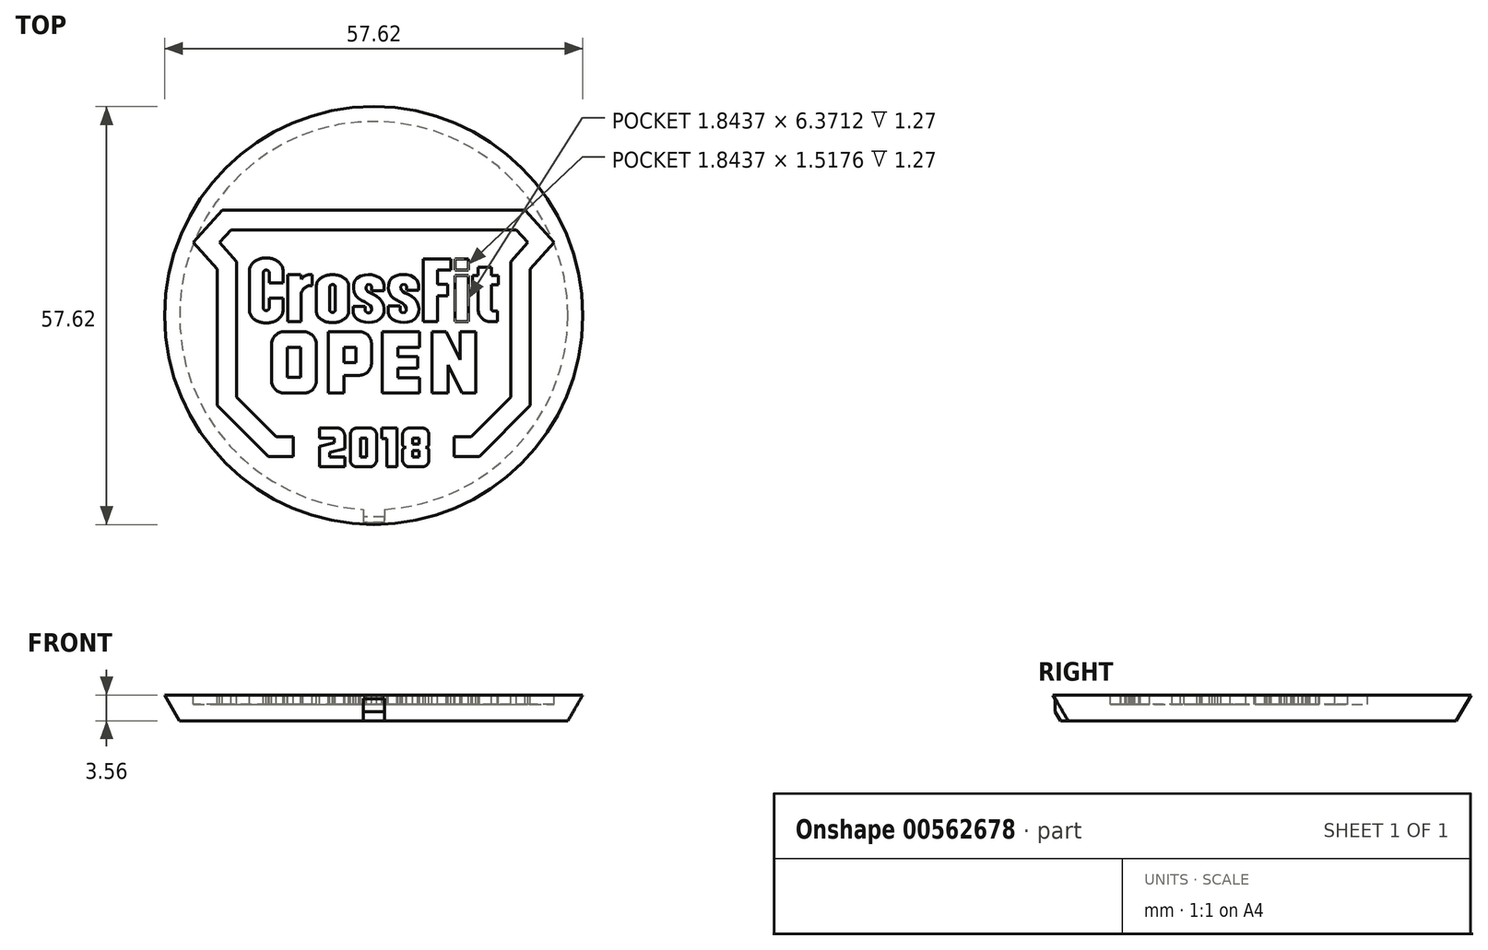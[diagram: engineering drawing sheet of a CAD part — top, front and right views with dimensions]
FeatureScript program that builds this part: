
annotation { "Feature Type Name" : "Feature", "Feature Type Description" : "" }
export const myFeature = defineFeature(function(context is Context, id is Id, definition is map)
    precondition{}
    {
        {
            var Q0;
            Q0=qCreatedBy(makeId("Top.planeOp"),FACE);
            var sketch = newSketch(context, id + "F0", { "sketchPlane" : qUnion([Q0])});
            skCircle(sketch, "E0", {"center": v(0, 0) * mm, "radius": 28.96 * mm});
            skSolve(sketch);
        }
        {
            var Q0;
            Q0=makeQuery(id+"F0.imprint","IMPRINT",FACE,{"disambiguationData":[TD([[makeQuery(id+"F0.imprint","IMPRINT",EDGE,{"derivedFrom":sQuery(id+"F0.wireOp",EDGE,"E0")}),1.0]])]});
            extrude(context, id + "F1", {"entities" : qUnion([Q0]), "depth" : 3.56 * mm, "offsetDistance" : 25.4 * mm});
        }
        {
            var Q0;
            Q0=makeQuery(id+"F1.opExtrude","CAP_FACE",FACE,{"disambiguationData":[OSD([sQuery(id+"F0.wireOp",EDGE,"E0")])],"isStart":false});
            var sketch = newSketch(context, id + "F2", { "sketchPlane" : qUnion([Q0])});
            skPoint(sketch, "E1", {"position": v(0.13, -0.67) * mm});
            skLineSegment(sketch, "E2", {"start": v(-15.2, 14.53) * mm, "end": v(-15.2, 11.82) * mm});
            skLineSegment(sketch, "E3", {"start": v(-15.2, 11.82) * mm, "end": v(-19.67, 11.82) * mm});
            skLineSegment(sketch, "E4", {"start": v(-19.67, 11.82) * mm, "end": v(-21.25, 10.06) * mm});
            skLineSegment(sketch, "E5", {"start": v(-21.25, 10.06) * mm, "end": v(-18.9, 7.43) * mm});
            skLineSegment(sketch, "E6", {"start": v(-18.9, 7.43) * mm, "end": v(-18.9, -11.25) * mm});
            skLineSegment(sketch, "E7", {"start": v(-18.9, -11.25) * mm, "end": v(-13.44, -16.74) * mm});
            skLineSegment(sketch, "E8", {"start": v(-13.44, -16.74) * mm, "end": v(-11.07, -16.74) * mm});
            skLineSegment(sketch, "E9", {"start": v(-11.07, -16.74) * mm, "end": v(-11.07, -19.45) * mm});
            skLineSegment(sketch, "E10", {"start": v(-11.07, -19.45) * mm, "end": v(-14.54, -19.45) * mm});
            skLineSegment(sketch, "E11", {"start": v(-14.54, -19.45) * mm, "end": v(-21.55, -12.4) * mm});
            skLineSegment(sketch, "E12", {"start": v(-21.55, -12.4) * mm, "end": v(-21.55, 6.37) * mm});
            skLineSegment(sketch, "E13", {"start": v(-21.55, 6.37) * mm, "end": v(-24.85, 10.06) * mm});
            skLineSegment(sketch, "E14", {"start": v(-24.85, 10.06) * mm, "end": v(-20.84, 14.53) * mm});
            skLineSegment(sketch, "E15", {"start": v(-20.84, 14.53) * mm, "end": v(-15.2, 14.53) * mm});
            skLineSegment(sketch, "E16", {"start": v(-14.42, 6) * mm, "end": v(-14.42, 4.47) * mm});
            skLineSegment(sketch, "E17", {"start": v(-14.42, 4.47) * mm, "end": v(-12.48, 4.47) * mm});
            skLineSegment(sketch, "E18", {"start": v(-12.48, 4.47) * mm, "end": v(-12.48, 6.3) * mm});
            skLineSegment(sketch, "E19", {"start": v(-17.15, 6.3) * mm, "end": v(-17.15, 0.62) * mm});
            skLineSegment(sketch, "E20", {"start": v(-14.42, 1) * mm, "end": v(-14.42, 2.43) * mm});
            skLineSegment(sketch, "E21", {"start": v(-14.42, 2.43) * mm, "end": v(-12.48, 2.43) * mm});
            skLineSegment(sketch, "E22", {"start": v(-12.48, 2.43) * mm, "end": v(-12.48, 0.62) * mm});
            skLineSegment(sketch, "E23", {"start": v(-15.2, 6) * mm, "end": v(-15.2, 1) * mm});
            skArc(sketch, "E24", {"start": v(-14.42, 6) * mm, "mid": v(-14.81, 6.27) * mm, "end": v(-15.2, 6) * mm});
            skArc(sketch, "E25", {"start": v(-15.2, 1) * mm, "mid": v(-14.81, 0.68) * mm, "end": v(-14.42, 1) * mm});
            skLineSegment(sketch, "E26", {"start": v(-9.97, 5) * mm, "end": v(-10.1, 5.63) * mm});
            skLineSegment(sketch, "E27", {"start": v(-10.1, 5.63) * mm, "end": v(-11.83, 5.63) * mm});
            skLineSegment(sketch, "E28", {"start": v(-11.83, 5.63) * mm, "end": v(-11.83, -0.85) * mm});
            skLineSegment(sketch, "E29", {"start": v(-11.83, -0.85) * mm, "end": v(-9.98, -0.85) * mm});
            skLineSegment(sketch, "E30", {"start": v(-9.98, -0.85) * mm, "end": v(-9.98, 3.1) * mm});
            skLineSegment(sketch, "E31", {"start": v(-8.5, 5.65) * mm, "end": v(-8.5, 4.11) * mm});
            skArc(sketch, "E32", {"start": v(-8.5, 5.65) * mm, "mid": v(-9.32, 5.53) * mm, "end": v(-9.97, 5) * mm});
            skArc(sketch, "E33", {"start": v(-8.5, 4.11) * mm, "mid": v(-9.44, 3.9) * mm, "end": v(-9.98, 3.1) * mm});
            skLineSegment(sketch, "E34", {"start": v(-7.89, 4.2) * mm, "end": v(-7.89, 0.46) * mm});
            skLineSegment(sketch, "E35", {"start": v(-3.47, 4.2) * mm, "end": v(-3.47, 0.46) * mm});
            skLineSegment(sketch, "E36", {"start": v(-6.05, 4.04) * mm, "end": v(-6.05, 0.68) * mm});
            skLineSegment(sketch, "E37", {"start": v(-5.3, 0.68) * mm, "end": v(-5.3, 4.04) * mm});
            skArc(sketch, "E38", {"start": v(-5.3, 4.04) * mm, "mid": v(-5.68, 4.28) * mm, "end": v(-6.05, 4.04) * mm});
            skArc(sketch, "E39", {"start": v(-6.05, 0.68) * mm, "mid": v(-5.68, 0.43) * mm, "end": v(-5.3, 0.68) * mm});
            skLineSegment(sketch, "E40", {"start": v(-5.68, 3.86) * mm, "end": v(-5.68, 0.84) * mm, "construction": true});
            skLineSegment(sketch, "E41", {"start": v(-7.89, 2.33) * mm, "end": v(-3.47, 2.33) * mm, "construction": true});
            skFitSpline(sketch, "E42.MirrorCS", {"points": [v(-3.47, 4.2) * mm, v(-3.93, 5.06) * mm, v(-4.62, 5.46) * mm, v(-5.68, 5.64) * mm], "startDerivative": vector(-0.46, 3.85) * mm, "endDerivative": vector(-4.22, 0.16) * mm});
            skFitSpline(sketch, "E43.MirrorCS", {"points": [v(-7.89, 0.46) * mm, v(-7.42, -0.4) * mm, v(-6.74, -0.8) * mm, v(-5.68, -0.98) * mm], "startDerivative": vector(0.46, -3.85) * mm, "endDerivative": vector(4.22, -0.16) * mm});
            skFitSpline(sketch, "E44.MirrorCS", {"points": [v(-3.47, 0.46) * mm, v(-3.93, -0.4) * mm, v(-4.62, -0.8) * mm, v(-5.68, -0.98) * mm], "startDerivative": vector(-0.46, -3.85) * mm, "endDerivative": vector(-4.22, -0.16) * mm});
            skFitSpline(sketch, "E45", {"points": [v(-17.15, 6.3) * mm, v(-16.64, 7.26) * mm, v(-16, 7.69) * mm, v(-14.81, 7.96) * mm], "startDerivative": vector(0.97, 4.15) * mm, "endDerivative": vector(4.22, 0.16) * mm});
            skLineSegment(sketch, "E46", {"start": v(-14.81, 5.84) * mm, "end": v(-14.81, 1.08) * mm, "construction": true});
            skFitSpline(sketch, "E47.MirrorCS", {"points": [v(-12.48, 6.3) * mm, v(-12.99, 7.26) * mm, v(-13.62, 7.69) * mm, v(-14.81, 7.96) * mm], "startDerivative": vector(-0.97, 4.15) * mm, "endDerivative": vector(-4.22, 0.16) * mm});
            skLineSegment(sketch, "E48", {"start": v(-17.15, 3.46) * mm, "end": v(-14.81, 3.46) * mm, "construction": true});
            skFitSpline(sketch, "E49.MirrorCS", {"points": [v(-17.15, 0.62) * mm, v(-16.64, -0.34) * mm, v(-16, -0.77) * mm, v(-14.81, -1.04) * mm], "startDerivative": vector(0.97, -4.15) * mm, "endDerivative": vector(4.22, -0.16) * mm});
            skFitSpline(sketch, "E50.MirrorCS", {"points": [v(-12.48, 0.62) * mm, v(-12.99, -0.34) * mm, v(-13.62, -0.77) * mm, v(-14.81, -1.04) * mm], "startDerivative": vector(-0.97, -4.15) * mm, "endDerivative": vector(-4.22, -0.16) * mm});
            skFitSpline(sketch, "E51.MirrorCS", {"points": [v(-7.89, 4.2) * mm, v(-7.42, 5.06) * mm, v(-6.74, 5.46) * mm, v(-5.68, 5.64) * mm], "startDerivative": vector(0.46, 3.85) * mm, "endDerivative": vector(4.22, 0.16) * mm});
            skLineSegment(sketch, "E52", {"start": v(-0.27, 4.07) * mm, "end": v(-0.27, 3.44) * mm});
            skLineSegment(sketch, "E53", {"start": v(-0.27, 3.44) * mm, "end": v(1.39, 3.44) * mm});
            skLineSegment(sketch, "E54", {"start": v(1.39, 3.44) * mm, "end": v(1.39, 4.25) * mm});
            skFitSpline(sketch, "E55", {"points": [v(1.39, 4.25) * mm, v(1.25, 4.73) * mm, v(0.96, 5.08) * mm, v(0.56, 5.36) * mm, v(0, 5.56) * mm, v(-0.4, 5.63) * mm, v(-0.7, 5.64) * mm, v(-1.07, 5.62) * mm, v(-1.62, 5.53) * mm, v(-2.03, 5.35) * mm, v(-2.4, 5.07) * mm, v(-2.62, 4.73) * mm, v(-2.76, 4.31) * mm, v(-2.8, 3.96) * mm, v(-2.78, 3.56) * mm, v(-2.7, 3.15) * mm, v(-2.47, 2.72) * mm, v(-2.25, 2.47) * mm, v(-1.97, 2.27) * mm, v(-1.61, 2.07) * mm, v(-1.3, 1.9) * mm, v(-1.02, 1.76) * mm, v(-0.75, 1.6) * mm, v(-0.5, 1.4) * mm, v(-0.41, 1.28) * mm, v(-0.32, 1.08) * mm, v(-0.3, 0.79) * mm, v(-0.34, 0.57) * mm, v(-0.46, 0.43) * mm, v(-0.64, 0.38) * mm, v(-0.84, 0.39) * mm, v(-1.03, 0.44) * mm, v(-1.16, 0.63) * mm], "startDerivative": vector(-2.14, 14.98) * mm, "endDerivative": vector(-3.94, 13.1) * mm});
            skLineSegment(sketch, "E56", {"start": v(-2.83, 0.39) * mm, "end": v(-2.83, 1.28) * mm});
            skLineSegment(sketch, "E57", {"start": v(-2.83, 1.28) * mm, "end": v(-1.16, 1.28) * mm});
            skLineSegment(sketch, "E58", {"start": v(-1.16, 1.28) * mm, "end": v(-1.16, 0.63) * mm});
            skFitSpline(sketch, "E59", {"points": [v(-2.83, 0.39) * mm, v(-2.67, -0.07) * mm, v(-2.35, -0.45) * mm, v(-1.98, -0.69) * mm, v(-1.5, -0.86) * mm, v(-1.03, -0.94) * mm, v(-0.7, -0.95) * mm, v(-0.34, -0.94) * mm, v(0.21, -0.84) * mm, v(0.6, -0.67) * mm, v(0.97, -0.39) * mm, v(1.22, -0.06) * mm, v(1.37, 0.3) * mm, v(1.42, 0.75) * mm, v(1.4, 1.11) * mm, v(1.3, 1.54) * mm, v(1.1, 1.95) * mm, v(0.87, 2.26) * mm, v(0.6, 2.5) * mm, v(0.3, 2.7) * mm, v(0, 2.88) * mm, v(-0.33, 3.05) * mm, v(-0.58, 3.18) * mm, v(-0.81, 3.31) * mm, v(-0.96, 3.44) * mm, v(-1.07, 3.64) * mm, v(-1.08, 3.86) * mm, v(-1.06, 4.07) * mm, v(-0.94, 4.24) * mm, v(-0.75, 4.3) * mm, v(-0.56, 4.29) * mm, v(-0.4, 4.23) * mm, v(-0.27, 4.07) * mm], "startDerivative": vector(2.14, -14.98) * mm, "endDerivative": vector(3.94, -13.1) * mm});
            skLineSegment(sketch, "E60", {"start": v(4.54, 4.08) * mm, "end": v(4.54, 3.45) * mm});
            skLineSegment(sketch, "E61", {"start": v(4.54, 3.45) * mm, "end": v(6.2, 3.45) * mm});
            skLineSegment(sketch, "E62", {"start": v(6.2, 3.45) * mm, "end": v(6.2, 4.26) * mm});
            skFitSpline(sketch, "E63", {"points": [v(6.2, 4.26) * mm, v(6.06, 4.74) * mm, v(5.77, 5.1) * mm, v(5.37, 5.37) * mm, v(4.81, 5.57) * mm, v(4.4, 5.64) * mm, v(4.11, 5.65) * mm, v(3.74, 5.63) * mm, v(3.2, 5.54) * mm, v(2.78, 5.36) * mm, v(2.42, 5.08) * mm, v(2.2, 4.74) * mm, v(2.05, 4.32) * mm, v(2.02, 3.97) * mm, v(2.03, 3.57) * mm, v(2.11, 3.16) * mm, v(2.34, 2.73) * mm, v(2.56, 2.48) * mm, v(2.84, 2.28) * mm, v(3.2, 2.08) * mm, v(3.52, 1.92) * mm, v(3.8, 1.77) * mm, v(4.06, 1.6) * mm, v(4.3, 1.41) * mm, v(4.4, 1.3) * mm, v(4.5, 1.09) * mm, v(4.5, 0.8) * mm, v(4.47, 0.58) * mm, v(4.35, 0.44) * mm, v(4.17, 0.39) * mm, v(3.97, 0.4) * mm, v(3.78, 0.45) * mm, v(3.65, 0.64) * mm], "startDerivative": vector(-2.14, 14.98) * mm, "endDerivative": vector(-3.94, 13.1) * mm});
            skLineSegment(sketch, "E64", {"start": v(1.98, 0.4) * mm, "end": v(1.98, 1.3) * mm});
            skLineSegment(sketch, "E65", {"start": v(1.98, 1.3) * mm, "end": v(3.65, 1.3) * mm});
            skLineSegment(sketch, "E66", {"start": v(3.65, 1.3) * mm, "end": v(3.65, 0.64) * mm});
            skFitSpline(sketch, "E67", {"points": [v(1.98, 0.4) * mm, v(2.14, -0.06) * mm, v(2.46, -0.44) * mm, v(2.83, -0.68) * mm, v(3.31, -0.85) * mm, v(3.78, -0.93) * mm, v(4.12, -0.95) * mm, v(4.47, -0.93) * mm, v(5.02, -0.83) * mm, v(5.42, -0.66) * mm, v(5.78, -0.38) * mm, v(6.03, -0.05) * mm, v(6.18, 0.32) * mm, v(6.23, 0.76) * mm, v(6.2, 1.12) * mm, v(6.12, 1.55) * mm, v(5.92, 1.96) * mm, v(5.68, 2.27) * mm, v(5.4, 2.5) * mm, v(5.1, 2.71) * mm, v(4.8, 2.89) * mm, v(4.48, 3.06) * mm, v(4.23, 3.2) * mm, v(4, 3.32) * mm, v(3.85, 3.45) * mm, v(3.74, 3.65) * mm, v(3.73, 3.87) * mm, v(3.75, 4.08) * mm, v(3.87, 4.25) * mm, v(4.06, 4.3) * mm, v(4.25, 4.3) * mm, v(4.42, 4.24) * mm, v(4.54, 4.08) * mm], "startDerivative": vector(2.14, -14.98) * mm, "endDerivative": vector(3.94, -13.1) * mm});
            skLineSegment(sketch, "E68", {"start": v(10.61, 7.8) * mm, "end": v(6.85, 7.8) * mm});
            skLineSegment(sketch, "E69", {"start": v(6.85, 7.8) * mm, "end": v(6.85, -0.85) * mm});
            skLineSegment(sketch, "E70", {"start": v(6.85, -0.85) * mm, "end": v(8.77, -0.85) * mm});
            skLineSegment(sketch, "E71", {"start": v(8.77, -0.85) * mm, "end": v(8.77, 2.7) * mm});
            skLineSegment(sketch, "E72", {"start": v(8.77, 2.7) * mm, "end": v(10.16, 2.7) * mm});
            skLineSegment(sketch, "E73", {"start": v(10.16, 2.7) * mm, "end": v(10.16, 4.29) * mm});
            skLineSegment(sketch, "E74", {"start": v(10.16, 4.29) * mm, "end": v(8.77, 4.29) * mm});
            skLineSegment(sketch, "E75", {"start": v(8.77, 4.29) * mm, "end": v(8.77, 6.28) * mm});
            skLineSegment(sketch, "E76", {"start": v(8.77, 6.28) * mm, "end": v(10.61, 6.28) * mm});
            skLineSegment(sketch, "E77", {"start": v(10.61, 6.28) * mm, "end": v(10.61, 7.8) * mm});
            skLineSegment(sketch, "E78", {"start": v(11.2, 7.8) * mm, "end": v(13.03, 7.8) * mm});
            skLineSegment(sketch, "E79", {"start": v(13.03, 7.8) * mm, "end": v(13.03, 6.28) * mm});
            skLineSegment(sketch, "E80", {"start": v(13.03, 6.28) * mm, "end": v(11.2, 6.28) * mm});
            skLineSegment(sketch, "E81", {"start": v(11.2, 6.28) * mm, "end": v(11.2, 7.8) * mm});
            skLineSegment(sketch, "E82", {"start": v(11.2, 5.52) * mm, "end": v(13.03, 5.52) * mm});
            skLineSegment(sketch, "E83", {"start": v(13.03, 5.52) * mm, "end": v(13.03, -0.85) * mm});
            skLineSegment(sketch, "E84", {"start": v(13.03, -0.85) * mm, "end": v(11.2, -0.85) * mm});
            skLineSegment(sketch, "E85", {"start": v(11.2, -0.85) * mm, "end": v(11.2, 5.52) * mm});
            skLineSegment(sketch, "E86", {"start": v(14.38, 6.63) * mm, "end": v(16.2, 6.63) * mm});
            skLineSegment(sketch, "E87", {"start": v(16.2, 6.63) * mm, "end": v(16.2, 5.52) * mm});
            skLineSegment(sketch, "E88", {"start": v(16.2, 5.52) * mm, "end": v(17.15, 5.52) * mm});
            skLineSegment(sketch, "E89", {"start": v(17.15, 5.52) * mm, "end": v(17.15, 4.23) * mm});
            skLineSegment(sketch, "E90", {"start": v(17.15, 4.23) * mm, "end": v(16.2, 4.23) * mm});
            skLineSegment(sketch, "E91", {"start": v(16.2, 4.23) * mm, "end": v(16.2, 0.92) * mm});
            skLineSegment(sketch, "E92", {"start": v(14.38, 6.63) * mm, "end": v(14.38, 5.52) * mm});
            skLineSegment(sketch, "E93", {"start": v(14.38, 5.52) * mm, "end": v(13.6, 5.52) * mm});
            skLineSegment(sketch, "E94", {"start": v(13.6, 5.52) * mm, "end": v(13.6, 4.23) * mm});
            skLineSegment(sketch, "E95", {"start": v(13.6, 4.23) * mm, "end": v(14.38, 4.23) * mm});
            skLineSegment(sketch, "E96", {"start": v(14.38, 4.23) * mm, "end": v(14.38, 0.85) * mm});
            skLineSegment(sketch, "E97", {"start": v(16.51, 0.61) * mm, "end": v(17.08, 0.61) * mm});
            skLineSegment(sketch, "E98", {"start": v(17.08, 0.61) * mm, "end": v(17.08, -0.85) * mm});
            skLineSegment(sketch, "E99", {"start": v(17.08, -0.85) * mm, "end": v(16.09, -0.85) * mm});
            skArc(sketch, "E100", {"start": v(14.38, 0.85) * mm, "mid": v(14.88, -0.35) * mm, "end": v(16.09, -0.85) * mm});
            skArc(sketch, "E101", {"start": v(16.2, 0.92) * mm, "mid": v(16.3, 0.7) * mm, "end": v(16.51, 0.61) * mm});
            skLineSegment(sketch, "E102", {"start": v(0, 18.62) * mm, "end": v(0, -25.74) * mm, "construction": true});
            skLineSegment(sketch, "E103.MirrorCS", {"start": v(15.2, 14.53) * mm, "end": v(15.2, 11.82) * mm});
            skLineSegment(sketch, "E104.MirrorCS", {"start": v(20.84, 14.53) * mm, "end": v(15.2, 14.53) * mm});
            skLineSegment(sketch, "E105.MirrorCS", {"start": v(24.85, 10.06) * mm, "end": v(20.84, 14.53) * mm});
            skLineSegment(sketch, "E106.MirrorCS", {"start": v(21.55, 6.37) * mm, "end": v(24.85, 10.06) * mm});
            skLineSegment(sketch, "E107.MirrorCS", {"start": v(21.55, -12.4) * mm, "end": v(21.55, 6.37) * mm});
            skLineSegment(sketch, "E108.MirrorCS", {"start": v(14.54, -19.45) * mm, "end": v(21.55, -12.4) * mm});
            skLineSegment(sketch, "E109.MirrorCS", {"start": v(11.07, -19.45) * mm, "end": v(14.54, -19.45) * mm});
            skLineSegment(sketch, "E110.MirrorCS", {"start": v(11.07, -16.74) * mm, "end": v(11.07, -19.45) * mm});
            skLineSegment(sketch, "E111.MirrorCS", {"start": v(13.44, -16.74) * mm, "end": v(11.07, -16.74) * mm});
            skLineSegment(sketch, "E112.MirrorCS", {"start": v(18.9, -11.25) * mm, "end": v(13.44, -16.74) * mm});
            skLineSegment(sketch, "E113.MirrorCS", {"start": v(18.9, 7.43) * mm, "end": v(18.9, -11.25) * mm});
            skLineSegment(sketch, "E114.MirrorCS", {"start": v(21.25, 10.06) * mm, "end": v(18.9, 7.43) * mm});
            skLineSegment(sketch, "E115.MirrorCS", {"start": v(19.67, 11.82) * mm, "end": v(21.25, 10.06) * mm});
            skLineSegment(sketch, "E116.MirrorCS", {"start": v(15.2, 11.82) * mm, "end": v(19.67, 11.82) * mm});
            skLineSegment(sketch, "E117", {"start": v(-5.1, -15.5) * mm, "end": v(-7.45, -15.5) * mm});
            skLineSegment(sketch, "E118", {"start": v(-7.45, -15.5) * mm, "end": v(-7.45, -16.87) * mm});
            skLineSegment(sketch, "E119", {"start": v(-7.45, -16.87) * mm, "end": v(-5.44, -16.87) * mm});
            skLineSegment(sketch, "E120", {"start": v(-5.44, -16.87) * mm, "end": v(-5.44, -17.52) * mm});
            skLineSegment(sketch, "E121", {"start": v(-5.44, -17.52) * mm, "end": v(-7.45, -18.02) * mm});
            skLineSegment(sketch, "E122", {"start": v(-7.45, -18.02) * mm, "end": v(-7.45, -20.86) * mm});
            skLineSegment(sketch, "E123", {"start": v(-7.45, -20.86) * mm, "end": v(-4, -20.86) * mm});
            skLineSegment(sketch, "E124", {"start": v(-4, -20.86) * mm, "end": v(-4, -19.5) * mm});
            skLineSegment(sketch, "E125", {"start": v(-4, -19.5) * mm, "end": v(-6.05, -19.5) * mm});
            skLineSegment(sketch, "E126", {"start": v(-6.05, -19.5) * mm, "end": v(-6.05, -18.84) * mm});
            skLineSegment(sketch, "E127", {"start": v(-6.05, -18.84) * mm, "end": v(-4, -18.34) * mm});
            skLineSegment(sketch, "E128", {"start": v(-4, -18.34) * mm, "end": v(-4, -16.6) * mm});
            skArc(sketch, "E129", {"start": v(-4, -16.6) * mm, "mid": v(-4.32, -15.83) * mm, "end": v(-5.1, -15.5) * mm});
            skLineSegment(sketch, "E130", {"start": v(-2.29, -15.5) * mm, "end": v(-0.56, -15.5) * mm});
            skLineSegment(sketch, "E131", {"start": v(-3.24, -16.46) * mm, "end": v(-3.24, -19.9) * mm});
            skLineSegment(sketch, "E132", {"start": v(-2.29, -20.86) * mm, "end": v(-0.56, -20.86) * mm});
            skLineSegment(sketch, "E133", {"start": v(0.4, -16.46) * mm, "end": v(0.4, -19.9) * mm});
            skArc(sketch, "E134", {"start": v(-2.29, -15.5) * mm, "mid": v(-2.96, -15.78) * mm, "end": v(-3.24, -16.46) * mm});
            skArc(sketch, "E135", {"start": v(0.4, -16.46) * mm, "mid": v(0.12, -15.78) * mm, "end": v(-0.56, -15.5) * mm});
            skArc(sketch, "E136", {"start": v(-3.24, -19.9) * mm, "mid": v(-2.96, -20.58) * mm, "end": v(-2.29, -20.86) * mm});
            skArc(sketch, "E137", {"start": v(-0.56, -20.86) * mm, "mid": v(0.12, -20.58) * mm, "end": v(0.4, -19.9) * mm});
            skLineSegment(sketch, "E138", {"start": v(1.1, -15.5) * mm, "end": v(3.22, -15.5) * mm});
            skLineSegment(sketch, "E139", {"start": v(3.22, -15.5) * mm, "end": v(3.22, -20.86) * mm});
            skLineSegment(sketch, "E140", {"start": v(3.22, -20.86) * mm, "end": v(1.77, -20.86) * mm});
            skLineSegment(sketch, "E141", {"start": v(1.77, -20.86) * mm, "end": v(1.77, -16.97) * mm});
            skLineSegment(sketch, "E142", {"start": v(1.77, -16.97) * mm, "end": v(1.1, -16.97) * mm});
            skLineSegment(sketch, "E143", {"start": v(1.1, -16.97) * mm, "end": v(1.1, -15.5) * mm});
            skLineSegment(sketch, "E144", {"start": v(-1.85, -16.87) * mm, "end": v(-0.99, -16.87) * mm});
            skLineSegment(sketch, "E145", {"start": v(-0.99, -16.87) * mm, "end": v(-0.99, -19.51) * mm});
            skLineSegment(sketch, "E146", {"start": v(-0.99, -19.51) * mm, "end": v(-1.85, -19.51) * mm});
            skLineSegment(sketch, "E147", {"start": v(-1.85, -19.51) * mm, "end": v(-1.85, -16.87) * mm});
            skLineSegment(sketch, "E148", {"start": v(-15.2, 14.53) * mm, "end": v(15.2, 14.53) * mm});
            skLineSegment(sketch, "E149", {"start": v(-15.2, 11.82) * mm, "end": v(15.2, 11.82) * mm});
            skLineSegment(sketch, "E150", {"start": v(-14.1, -4.04) * mm, "end": v(-14.1, -8.95) * mm});
            skLineSegment(sketch, "E151", {"start": v(-12.3, -10.7) * mm, "end": v(-9.74, -10.7) * mm});
            skLineSegment(sketch, "E152", {"start": v(-7.9, -8.95) * mm, "end": v(-7.9, -4.04) * mm});
            skLineSegment(sketch, "E153", {"start": v(-12.3, -2.22) * mm, "end": v(-9.74, -2.22) * mm});
            skArc(sketch, "E154", {"start": v(-12.3, -2.22) * mm, "mid": v(-13.57, -2.77) * mm, "end": v(-14.1, -4.04) * mm});
            skArc(sketch, "E155", {"start": v(-7.9, -4.04) * mm, "mid": v(-8.44, -2.75) * mm, "end": v(-9.74, -2.22) * mm});
            skArc(sketch, "E156", {"start": v(-9.74, -10.7) * mm, "mid": v(-8.44, -10.22) * mm, "end": v(-7.9, -8.95) * mm});
            skArc(sketch, "E157", {"start": v(-14.1, -8.95) * mm, "mid": v(-13.55, -10.19) * mm, "end": v(-12.3, -10.7) * mm});
            skLineSegment(sketch, "E158.bottom", {"start": v(-11.9, -4.38) * mm, "end": v(-10.07, -4.38) * mm});
            skLineSegment(sketch, "E158.top", {"start": v(-11.9, -8.53) * mm, "end": v(-10.07, -8.53) * mm});
            skLineSegment(sketch, "E158.left", {"start": v(-11.9, -4.38) * mm, "end": v(-11.9, -8.53) * mm});
            skLineSegment(sketch, "E158.right", {"start": v(-10.07, -4.38) * mm, "end": v(-10.07, -8.53) * mm});
            skLineSegment(sketch, "E159", {"start": v(-6.28, -2.22) * mm, "end": v(-6.28, -10.7) * mm});
            skLineSegment(sketch, "E160", {"start": v(-6.28, -10.7) * mm, "end": v(-4.11, -10.7) * mm});
            skLineSegment(sketch, "E161", {"start": v(-4.11, -10.7) * mm, "end": v(-4.11, -8.24) * mm});
            skLineSegment(sketch, "E162", {"start": v(-4.11, -8.24) * mm, "end": v(-2.07, -8.24) * mm});
            skLineSegment(sketch, "E163", {"start": v(-6.28, -2.22) * mm, "end": v(-2.07, -2.22) * mm});
            skLineSegment(sketch, "E164", {"start": v(-0.3, -3.92) * mm, "end": v(-0.3, -6.53) * mm});
            skArc(sketch, "E165", {"start": v(-0.3, -3.92) * mm, "mid": v(-0.83, -2.7) * mm, "end": v(-2.07, -2.22) * mm});
            skArc(sketch, "E166", {"start": v(-2.07, -8.24) * mm, "mid": v(-0.83, -7.76) * mm, "end": v(-0.3, -6.53) * mm});
            skLineSegment(sketch, "E167.bottom", {"start": v(-4.13, -4.4) * mm, "end": v(-2.47, -4.4) * mm});
            skLineSegment(sketch, "E167.top", {"start": v(-4.13, -6.49) * mm, "end": v(-2.47, -6.49) * mm});
            skLineSegment(sketch, "E167.left", {"start": v(-4.13, -4.4) * mm, "end": v(-4.13, -6.49) * mm});
            skLineSegment(sketch, "E167.right", {"start": v(-2.47, -4.4) * mm, "end": v(-2.47, -6.49) * mm});
            skLineSegment(sketch, "E168", {"start": v(1.15, -2.22) * mm, "end": v(1.15, -10.7) * mm});
            skLineSegment(sketch, "E169", {"start": v(1.15, -10.7) * mm, "end": v(6.3, -10.7) * mm});
            skLineSegment(sketch, "E170", {"start": v(6.3, -10.7) * mm, "end": v(6.3, -8.56) * mm});
            skLineSegment(sketch, "E171", {"start": v(6.3, -8.56) * mm, "end": v(3.35, -8.56) * mm});
            skLineSegment(sketch, "E172", {"start": v(3.35, -8.56) * mm, "end": v(3.35, -7.26) * mm});
            skLineSegment(sketch, "E173", {"start": v(3.35, -7.26) * mm, "end": v(6.04, -7.26) * mm});
            skLineSegment(sketch, "E174", {"start": v(6.04, -7.26) * mm, "end": v(6.04, -5.67) * mm});
            skLineSegment(sketch, "E175", {"start": v(6.04, -5.67) * mm, "end": v(3.35, -5.66) * mm});
            skLineSegment(sketch, "E176", {"start": v(3.35, -5.66) * mm, "end": v(3.35, -4.36) * mm});
            skLineSegment(sketch, "E177", {"start": v(3.35, -4.36) * mm, "end": v(6.3, -4.36) * mm});
            skLineSegment(sketch, "E178", {"start": v(6.3, -4.36) * mm, "end": v(6.3, -2.22) * mm});
            skLineSegment(sketch, "E179", {"start": v(6.3, -2.22) * mm, "end": v(1.15, -2.22) * mm});
            skLineSegment(sketch, "E180", {"start": v(8.05, -2.22) * mm, "end": v(8.05, -10.7) * mm});
            skLineSegment(sketch, "E181", {"start": v(8.05, -10.7) * mm, "end": v(10.24, -10.7) * mm});
            skLineSegment(sketch, "E182", {"start": v(10.24, -10.7) * mm, "end": v(10.24, -6.84) * mm});
            skLineSegment(sketch, "E183", {"start": v(10.24, -6.84) * mm, "end": v(12.13, -10.7) * mm});
            skLineSegment(sketch, "E184", {"start": v(12.13, -10.7) * mm, "end": v(14.07, -10.7) * mm});
            skLineSegment(sketch, "E185", {"start": v(14.07, -10.7) * mm, "end": v(14.07, -2.22) * mm});
            skLineSegment(sketch, "E186", {"start": v(14.07, -2.22) * mm, "end": v(11.89, -2.22) * mm});
            skLineSegment(sketch, "E187", {"start": v(11.89, -2.22) * mm, "end": v(11.89, -6.08) * mm});
            skLineSegment(sketch, "E188", {"start": v(11.89, -6.08) * mm, "end": v(10, -2.22) * mm});
            skLineSegment(sketch, "E189", {"start": v(10, -2.22) * mm, "end": v(8.05, -2.22) * mm});
            skCircle(sketch, "E190", {"center": v(0, 0) * mm, "radius": 28.9 * mm});
            skLineSegment(sketch, "E191.MirrorCS", {"start": v(6.65, -15.5) * mm, "end": v(4.93, -15.5) * mm});
            skLineSegment(sketch, "E192.MirrorCS", {"start": v(7.6, -16.46) * mm, "end": v(7.6, -17.7) * mm});
            skArc(sketch, "E193.MirrorCS", {"start": v(6.65, -15.5) * mm, "mid": v(7.33, -15.78) * mm, "end": v(7.6, -16.46) * mm});
            skArc(sketch, "E194.MirrorCS", {"start": v(7.6, -19.9) * mm, "mid": v(7.33, -20.58) * mm, "end": v(6.65, -20.86) * mm});
            skLineSegment(sketch, "E195.MirrorCS", {"start": v(6.65, -20.86) * mm, "end": v(4.93, -20.86) * mm});
            skLineSegment(sketch, "E196.MirrorCS", {"start": v(3.97, -16.46) * mm, "end": v(3.97, -17.7) * mm});
            skArc(sketch, "E197.MirrorCS", {"start": v(4.93, -20.86) * mm, "mid": v(4.25, -20.58) * mm, "end": v(3.97, -19.9) * mm});
            skArc(sketch, "E198.MirrorCS", {"start": v(3.97, -16.46) * mm, "mid": v(4.25, -15.78) * mm, "end": v(4.93, -15.5) * mm});
            skLineSegment(sketch, "E199.MirrorCS", {"start": v(6.22, -16.87) * mm, "end": v(5.36, -16.87) * mm});
            skLineSegment(sketch, "E200.MirrorCS", {"start": v(6.22, -19.51) * mm, "end": v(6.22, -18.63) * mm});
            skLineSegment(sketch, "E201.MirrorCS", {"start": v(5.36, -16.87) * mm, "end": v(5.36, -17.74) * mm});
            skLineSegment(sketch, "E202.MirrorCS", {"start": v(5.36, -19.51) * mm, "end": v(6.22, -19.51) * mm});
            skLineSegment(sketch, "E203", {"start": v(5.36, -17.74) * mm, "end": v(6.22, -17.74) * mm});
            skLineSegment(sketch, "E204", {"start": v(6.22, -17.74) * mm, "end": v(6.22, -16.87) * mm});
            skLineSegment(sketch, "E205", {"start": v(5.36, -18.63) * mm, "end": v(6.22, -18.63) * mm});
            skLineSegment(sketch, "E206", {"start": v(5.36, -18.63) * mm, "end": v(5.36, -19.51) * mm});
            skArc(sketch, "E207", {"start": v(3.97, -17.7) * mm, "mid": v(4.11, -18.04) * mm, "end": v(4.45, -18.18) * mm});
            skArc(sketch, "E208.MirrorCS", {"start": v(7.6, -17.7) * mm, "mid": v(7.47, -18.04) * mm, "end": v(7.13, -18.18) * mm});
            skArc(sketch, "E209.MirrorCS", {"start": v(3.97, -18.66) * mm, "mid": v(4.11, -18.32) * mm, "end": v(4.45, -18.18) * mm});
            skArc(sketch, "E210.MirrorCS", {"start": v(7.6, -18.66) * mm, "mid": v(7.47, -18.32) * mm, "end": v(7.13, -18.18) * mm});
            skLineSegment(sketch, "E211", {"start": v(7.6, -18.66) * mm, "end": v(7.6, -19.9) * mm});
            skLineSegment(sketch, "E212", {"start": v(3.97, -18.66) * mm, "end": v(3.97, -19.9) * mm});
            skSolve(sketch);
        }
        {
            var Q0;
            Q0=makeQuery(id+"F2.imprint","IMPRINT",FACE,{"disambiguationData":[TD([[makeQuery(id+"F2.imprint","IMPRINT",EDGE,{"derivedFrom":sQuery(id+"F2.wireOp",EDGE,"E2")}),1.0]])]});
            var Q1;
            Q1=makeQuery(id+"F2.imprint","IMPRINT",FACE,{"disambiguationData":[TD([[makeQuery(id+"F2.imprint","IMPRINT",EDGE,{"derivedFrom":sQuery(id+"F2.wireOp",EDGE,"E103.MirrorCS")}),1.0]])]});
            var Q2;
            Q2=makeQuery(id+"F2.imprint","IMPRINT",FACE,{"disambiguationData":[TD([[makeQuery(id+"F2.imprint","IMPRINT",EDGE,{"derivedFrom":sQuery(id+"F2.wireOp",EDGE,"E2")}),-1.0]])]});
            var Q3;
            Q3=makeQuery(id+"F2.imprint","IMPRINT",FACE,{"disambiguationData":[TD([[makeQuery(id+"F2.imprint","IMPRINT",EDGE,{"derivedFrom":sQuery(id+"F2.wireOp",EDGE,"E16")}),1.0]])]});
            var Q4;
            Q4=makeQuery(id+"F2.imprint","IMPRINT",FACE,{"disambiguationData":[TD([[makeQuery(id+"F2.imprint","IMPRINT",EDGE,{"derivedFrom":sQuery(id+"F2.wireOp",EDGE,"E26")}),1.0]])]});
            var Q5;
            Q5=makeQuery(id+"F2.imprint","IMPRINT",FACE,{"disambiguationData":[TD([[makeQuery(id+"F2.imprint","IMPRINT",EDGE,{"derivedFrom":sQuery(id+"F2.wireOp",EDGE,"E34")}),1.0]])]});
            var Q6;
            Q6=makeQuery(id+"F2.imprint","IMPRINT",FACE,{"disambiguationData":[TD([[makeQuery(id+"F2.imprint","IMPRINT",EDGE,{"derivedFrom":sQuery(id+"F2.wireOp",EDGE,"E52")}),1.0]])]});
            var Q7;
            Q7=makeQuery(id+"F2.imprint","IMPRINT",FACE,{"disambiguationData":[TD([[makeQuery(id+"F2.imprint","IMPRINT",EDGE,{"derivedFrom":sQuery(id+"F2.wireOp",EDGE,"E60")}),1.0]])]});
            var Q8;
            Q8=makeQuery(id+"F2.imprint","IMPRINT",FACE,{"disambiguationData":[TD([[makeQuery(id+"F2.imprint","IMPRINT",EDGE,{"derivedFrom":sQuery(id+"F2.wireOp",EDGE,"E68")}),1.0]])]});
            var Q9;
            Q9=makeQuery(id+"F2.imprint","IMPRINT",FACE,{"disambiguationData":[TD([[makeQuery(id+"F2.imprint","IMPRINT",EDGE,{"derivedFrom":sQuery(id+"F2.wireOp",EDGE,"E82")}),-1.0]])]});
            var Q10;
            Q10=makeQuery(id+"F2.imprint","IMPRINT",FACE,{"disambiguationData":[TD([[makeQuery(id+"F2.imprint","IMPRINT",EDGE,{"derivedFrom":sQuery(id+"F2.wireOp",EDGE,"E78")}),-1.0]])]});
            var Q11;
            Q11=makeQuery(id+"F2.imprint","IMPRINT",FACE,{"disambiguationData":[TD([[makeQuery(id+"F2.imprint","IMPRINT",EDGE,{"derivedFrom":sQuery(id+"F2.wireOp",EDGE,"E86")}),-1.0]])]});
            var Q12;
            Q12=makeQuery(id+"F2.imprint","IMPRINT",FACE,{"disambiguationData":[TD([[makeQuery(id+"F2.imprint","IMPRINT",EDGE,{"derivedFrom":sQuery(id+"F2.wireOp",EDGE,"E180")}),1.0]])]});
            var Q13;
            Q13=makeQuery(id+"F2.imprint","IMPRINT",FACE,{"disambiguationData":[TD([[makeQuery(id+"F2.imprint","IMPRINT",EDGE,{"derivedFrom":sQuery(id+"F2.wireOp",EDGE,"E168")}),1.0]])]});
            var Q14;
            Q14=makeQuery(id+"F2.imprint","IMPRINT",FACE,{"disambiguationData":[TD([[makeQuery(id+"F2.imprint","IMPRINT",EDGE,{"derivedFrom":sQuery(id+"F2.wireOp",EDGE,"E159")}),1.0]])]});
            var Q15;
            Q15=makeQuery(id+"F2.imprint","IMPRINT",FACE,{"disambiguationData":[TD([[makeQuery(id+"F2.imprint","IMPRINT",EDGE,{"derivedFrom":sQuery(id+"F2.wireOp",EDGE,"E150")}),1.0]])]});
            var Q16;
            Q16=makeQuery(id+"F2.imprint","IMPRINT",FACE,{"disambiguationData":[TD([[makeQuery(id+"F2.imprint","IMPRINT",EDGE,{"derivedFrom":sQuery(id+"F2.wireOp",EDGE,"E117")}),1.0]])]});
            var Q17;
            Q17=makeQuery(id+"F2.imprint","IMPRINT",FACE,{"disambiguationData":[TD([[makeQuery(id+"F2.imprint","IMPRINT",EDGE,{"derivedFrom":sQuery(id+"F2.wireOp",EDGE,"E130")}),-1.0]])]});
            var Q18;
            Q18=makeQuery(id+"F2.imprint","IMPRINT",FACE,{"disambiguationData":[TD([[makeQuery(id+"F2.imprint","IMPRINT",EDGE,{"derivedFrom":sQuery(id+"F2.wireOp",EDGE,"E138")}),-1.0]])]});
            var Q19;
            Q19=makeQuery(id+"F2.imprint","IMPRINT",FACE,{"disambiguationData":[TD([[makeQuery(id+"F2.imprint","IMPRINT",EDGE,{"derivedFrom":sQuery(id+"F2.wireOp",EDGE,"E191.MirrorCS")}),1.0]])]});
            extrude(context, id + "F3", {"entities" : qUnion([Q0, Q1, Q2, Q3, Q4, Q5, Q6, Q7, Q8, Q9, Q10, Q11, Q12, Q13, Q14, Q15, Q16, Q17, Q18, Q19]), "operationType" : NewBodyOperationType.REMOVE, "oppositeDirection" : true, "depth" : 1.27 * mm, "offsetDistance" : 25.4 * mm});
        }
        {
            var Q0;
            Q0=makeQuery(id+"F1.opExtrude","CAP_EDGE",EDGE,{"disambiguationData":[OSD([sQuery(id+"F0.wireOp",EDGE,"E0")])],"isStart":true});
            chamfer(context, id + "F4", {"entities" : qUnion([Q0]), "chamferType" : ChamferType.OFFSET_ANGLE, "width" : 3.8 * mm, "oppositeDirection" : false, "angle" : 30 * degree, "tangentPropagation" : true});
        }
        {
            var Q0;
            {var subQ0=sQuery(id+"F0.wireOp",EDGE,"E0");Q0=makeQuery(id+"F3.boolean.opBoolean","SPLIT",FACE,{"disambiguationData":[TD([makeQuery(id+"F1.opExtrude","SWEPT_FACE",FACE,{"disambiguationData":[OSD([subQ0])]})])],"derivedFrom":makeQuery(id+"F1.opExtrude","CAP_FACE",FACE,{"disambiguationData":[OSD([subQ0])],"isStart":false})});}
            var sketch = newSketch(context, id + "F5", { "sketchPlane" : qUnion([Q0])});
            skCircle(sketch, "E213.0", {"center": v(0, 0) * mm, "radius": 26.76 * mm});
            skLineSegment(sketch, "E214.bottom", {"start": v(-1.46, -28.5) * mm, "end": v(1.46, -28.5) * mm});
            skLineSegment(sketch, "E214.top", {"start": v(-1.46, -26.72) * mm, "end": v(1.46, -26.72) * mm});
            skLineSegment(sketch, "E214.left", {"start": v(-1.46, -28.5) * mm, "end": v(-1.46, -26.72) * mm});
            skLineSegment(sketch, "E214.right", {"start": v(1.46, -28.5) * mm, "end": v(1.46, -26.72) * mm});
            skSolve(sketch);
        }
        {
            var Q0;
            Q0=makeQuery(id+"F5.imprint","IMPRINT",FACE,{"disambiguationData":[TD([[makeQuery(id+"F5.imprint","IMPRINT",EDGE,{"derivedFrom":sQuery(id+"F5.wireOp",EDGE,"E214.bottom")}),1.0]])]});
            var Q1;
            Q1=makeQuery(id+"F1.opExtrude","CAP_FACE",FACE,{"disambiguationData":[OSD([sQuery(id+"F0.wireOp",EDGE,"E0")])],"isStart":true});
            extrude(context, id + "F6", {"entities" : qUnion([Q0]), "operationType" : NewBodyOperationType.ADD, "endBound" : BoundingType.UP_TO_SURFACE, "oppositeDirection" : true, "depth" : 25.4 * mm, "endBoundEntityFace" : qUnion([Q1]), "offsetDistance" : 0.25 * mm});
        }
        {
            var Q0;
            Q0=makeQuery(id+"F6.opExtrude","CAP_EDGE",EDGE,{"disambiguationData":[OSD([sQuery(id+"F5.wireOp",EDGE,"E214.bottom")])],"isStart":false});
            chamfer(context, id + "F7", {"entities" : qUnion([Q0]), "chamferType" : ChamferType.OFFSET_ANGLE, "width" : 1.27 * mm, "oppositeDirection" : true, "angle" : 30 * degree, "tangentPropagation" : true});
        }
    });
